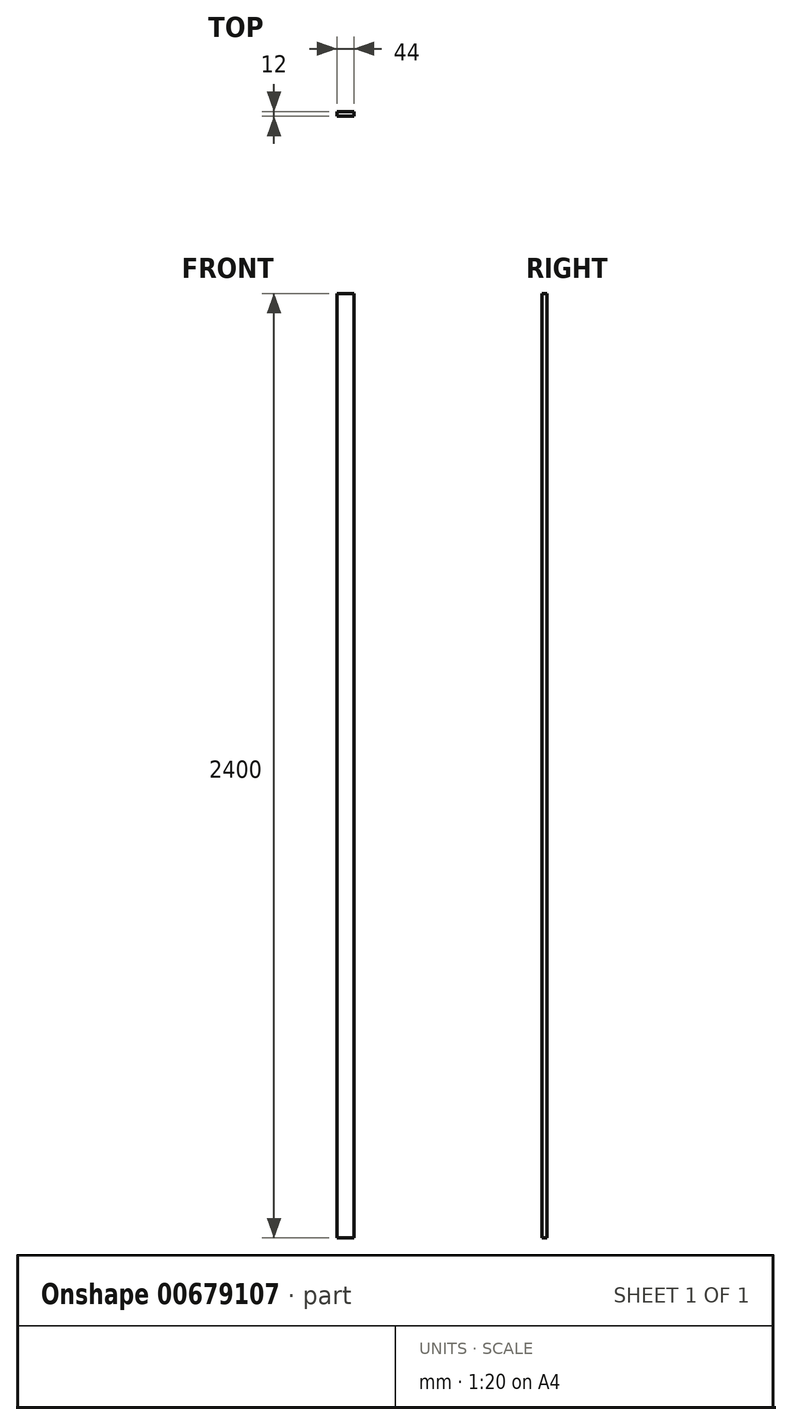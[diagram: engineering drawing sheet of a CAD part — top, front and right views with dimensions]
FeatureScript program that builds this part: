
annotation { "Feature Type Name" : "Feature", "Feature Type Description" : "" }
export const myFeature = defineFeature(function(context is Context, id is Id, definition is map)
    precondition{}
    {
        {
            var Q0;
            Q0=qCreatedBy(makeId("Top.planeOp"),FACE);
            var sketch = newSketch(context, id + "F0", { "sketchPlane" : qUnion([Q0])});
            skLineSegment(sketch, "E0.bottom", {"start": v(-14.62, 12) * mm, "end": v(29.38, 12) * mm});
            skLineSegment(sketch, "E0.top", {"start": v(-14.62, 0) * mm, "end": v(29.38, 0) * mm});
            skLineSegment(sketch, "E0.left", {"start": v(-14.62, 12) * mm, "end": v(-14.62, 0) * mm});
            skLineSegment(sketch, "E0.right", {"start": v(29.38, 12) * mm, "end": v(29.38, 0) * mm});
            skSolve(sketch);
        }
        {
            var Q0;
            Q0 = qSketchRegion(id + "F0", true);
            extrude(context, id + "F1", {"entities" : qUnion([Q0]), "depth" : 2400 * mm, "offsetDistance" : 25 * mm});
        }
    });
